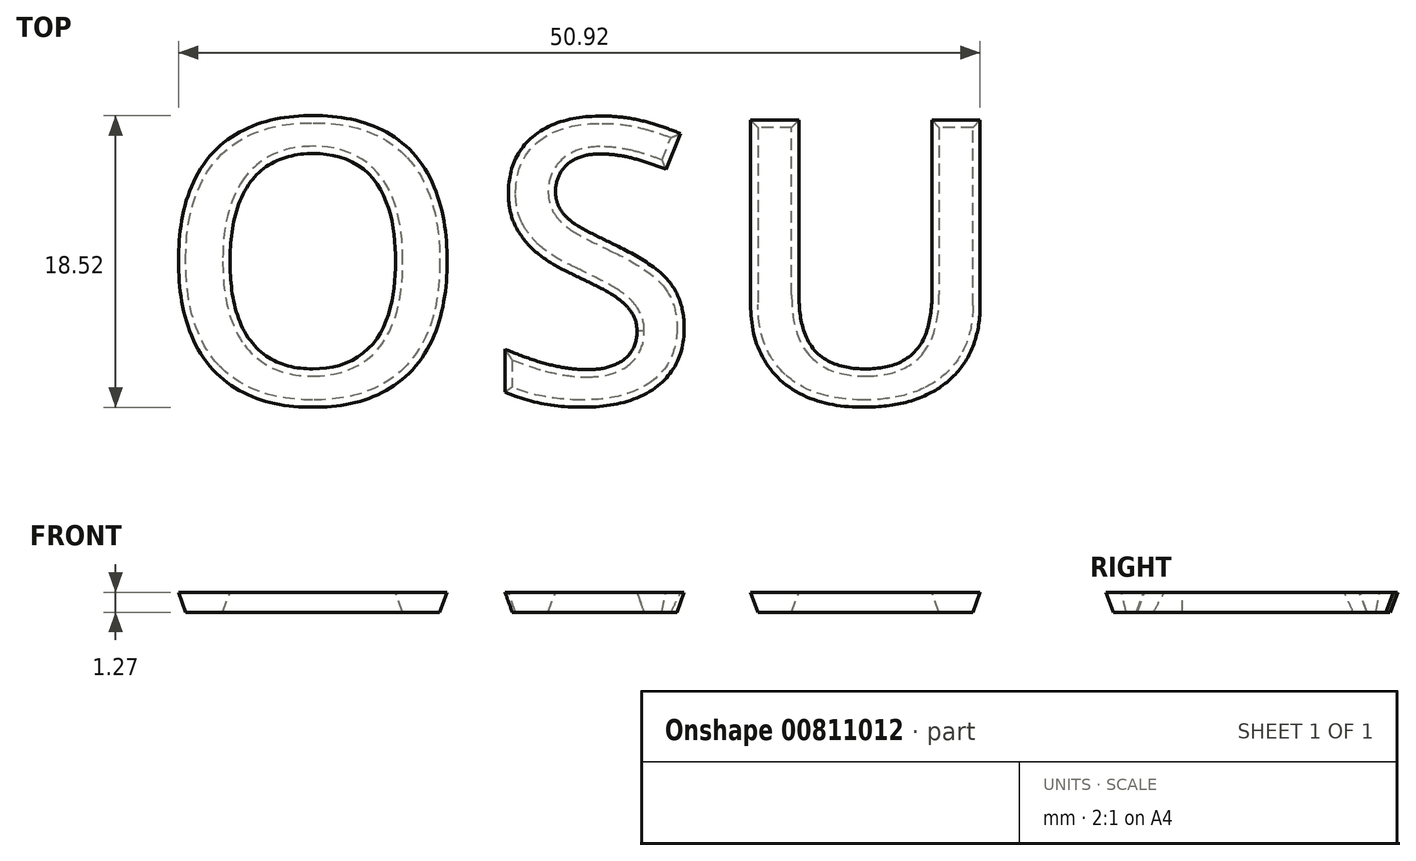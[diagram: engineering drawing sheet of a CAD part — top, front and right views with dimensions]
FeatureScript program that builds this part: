
annotation { "Feature Type Name" : "Feature", "Feature Type Description" : "" }
export const myFeature = defineFeature(function(context is Context, id is Id, definition is map)
    precondition{}
    {
        {
            var Q0;
            Q0=qCreatedBy(makeId("Top.planeOp"),FACE);
            var sketch = newSketch(context, id + "F0", { "sketchPlane" : qUnion([Q0])});
            skText(sketch, "E0", { "text": "OSU", "fontName": "OpenSans-Bold.ttf"});
            const initialGuessF0  = {"E0": [-0.02755, -0.00953, 1, 0, 0.01905]};
            skSetInitialGuess(sketch, initialGuessF0);
            skSolve(sketch);
        }
        {
            var Q0;
            Q0=makeQuery(id+"F0.imprint","IMPRINT",FACE,{"disambiguationData":[TD([[makeQuery(id+"F0.imprint","IMPRINT",EDGE,{"derivedFrom":sQuery(id+"F0.wireOp",EDGE,"E0.sketch_text.stroke-0")}),-1.0]])]});
            var Q1;
            Q1=makeQuery(id+"F0.imprint","IMPRINT",FACE,{"disambiguationData":[TD([[makeQuery(id+"F0.imprint","IMPRINT",EDGE,{"derivedFrom":sQuery(id+"F0.wireOp",EDGE,"E0.sketch_text.stroke-42")}),-1.0]])]});
            var Q2;
            Q2=makeQuery(id+"F0.imprint","IMPRINT",FACE,{"disambiguationData":[TD([[makeQuery(id+"F0.imprint","IMPRINT",EDGE,{"derivedFrom":sQuery(id+"F0.wireOp",EDGE,"E0.sketch_text.stroke-14")}),-1.0]])]});
            extrude(context, id + "F1", {"entities" : qUnion([Q0, Q1, Q2]), "oppositeDirection" : true, "depth" : 2.54 * mm, "offsetDistance" : 25.4 * mm, "hasDraft" : true, "draftAngle" : 20 * degree, "draftPullDirection" : true});
        }
        {
            var Q0;
            Q0=qCreatedBy(makeId("Top.planeOp"),FACE);
            var sketch = newSketch(context, id + "F2", { "sketchPlane" : qUnion([Q0])});
            skLineSegment(sketch, "E1.bottom", {"start": v(-34.81, 16.02) * mm, "end": v(33.03, 16.02) * mm});
            skLineSegment(sketch, "E1.top", {"start": v(-34.81, -15.13) * mm, "end": v(33.03, -15.13) * mm});
            skLineSegment(sketch, "E1.left", {"start": v(-34.81, 16.02) * mm, "end": v(-34.81, -15.13) * mm});
            skLineSegment(sketch, "E1.right", {"start": v(33.03, 16.02) * mm, "end": v(33.03, -15.13) * mm});
            skSolve(sketch);
        }
        {
            var Q0;
            Q0 = qSketchRegion(id + "F2", true);
            extrude(context, id + "F3", {"entities" : qUnion([Q0]), "operationType" : NewBodyOperationType.REMOVE, "oppositeDirection" : true, "depth" : 1.27 * mm, "offsetDistance" : 25.4 * mm});
        }
    });
